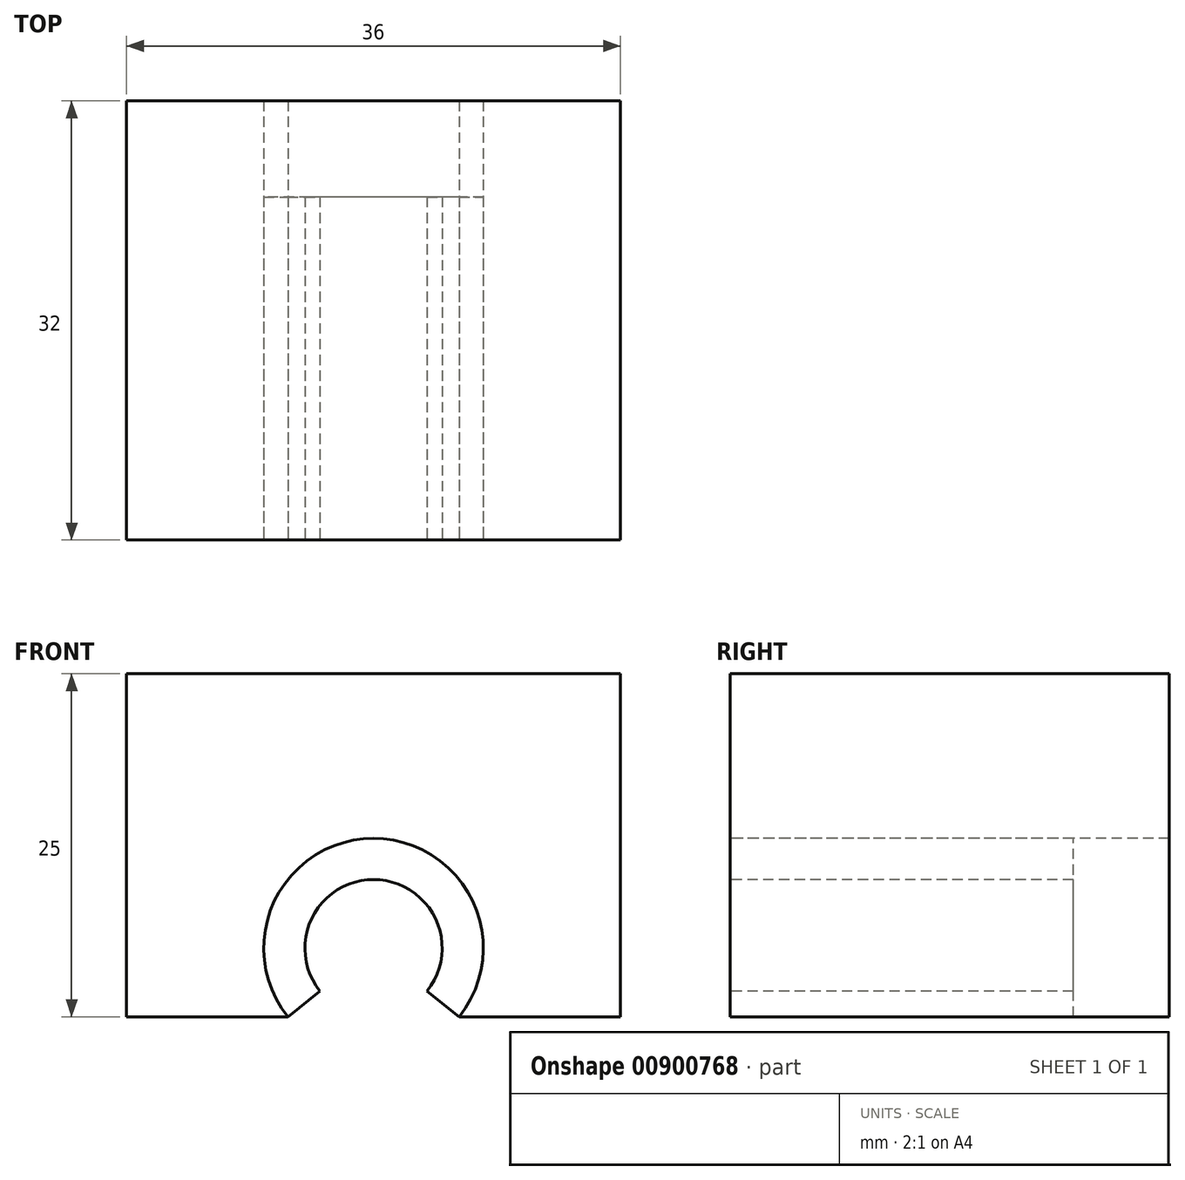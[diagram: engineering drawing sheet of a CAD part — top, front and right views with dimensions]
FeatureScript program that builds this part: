
annotation { "Feature Type Name" : "Feature", "Feature Type Description" : "" }
export const myFeature = defineFeature(function(context is Context, id is Id, definition is map)
    precondition{}
    {
        {
            var Q0;
            Q0=qCreatedBy(makeId("Front.planeOp"),FACE);
            var sketch = newSketch(context, id + "F0", { "sketchPlane" : qUnion([Q0])});
            skArc(sketch, "E0", {"start": v(3.9, -3.12) * mm, "mid": v(0, 5) * mm, "end": v(-3.9, -3.13) * mm});
            skArc(sketch, "E1", {"start": v(6.24, -5) * mm, "mid": v(0, 8) * mm, "end": v(-6.24, -5) * mm});
            skLineSegment(sketch, "E2", {"start": v(6.24, -5) * mm, "end": v(18, -5) * mm});
            skLineSegment(sketch, "E3", {"start": v(18, -5) * mm, "end": v(18, 20) * mm});
            skLineSegment(sketch, "E4", {"start": v(18, 20) * mm, "end": v(0, 20) * mm});
            skLineSegment(sketch, "E5", {"start": v(0, 20) * mm, "end": v(-18, 20) * mm});
            skLineSegment(sketch, "E6", {"start": v(-18, 20) * mm, "end": v(-18, -5) * mm});
            skLineSegment(sketch, "E7", {"start": v(-18, -5) * mm, "end": v(-6.24, -5) * mm});
            skLineSegment(sketch, "E8", {"start": v(-6.24, -5) * mm, "end": v(-3.9, -3.13) * mm});
            skLineSegment(sketch, "E9", {"start": v(6.24, -5) * mm, "end": v(3.9, -3.13) * mm});
            skLineSegment(sketch, "E10", {"start": v(0, 0) * mm, "end": v(3.9, -3.13) * mm, "construction": true});
            skSolve(sketch);
        }
        {
            var Q0;
            Q0=makeQuery(id+"F0.imprint","IMPRINT",FACE,{"disambiguationData":[TD([[makeQuery(id+"F0.imprint","IMPRINT",EDGE,{"derivedFrom":sQuery(id+"F0.wireOp",EDGE,"E1")}),-1.0]])]});
            extrude(context, id + "F1", {"entities" : qUnion([Q0]), "oppositeDirection" : true, "depth" : 32 * mm, "offsetDistance" : 25 * mm});
        }
        {
            var Q0;
            Q0=makeQuery(id+"F0.imprint","IMPRINT",FACE,{"disambiguationData":[TD([[makeQuery(id+"F0.imprint","IMPRINT",EDGE,{"derivedFrom":sQuery(id+"F0.wireOp",EDGE,"E0")}),-1.0]])]});
            extrude(context, id + "F2", {"entities" : qUnion([Q0]), "oppositeDirection" : true, "depth" : 25 * mm, "offsetDistance" : 25 * mm});
        }
    });
